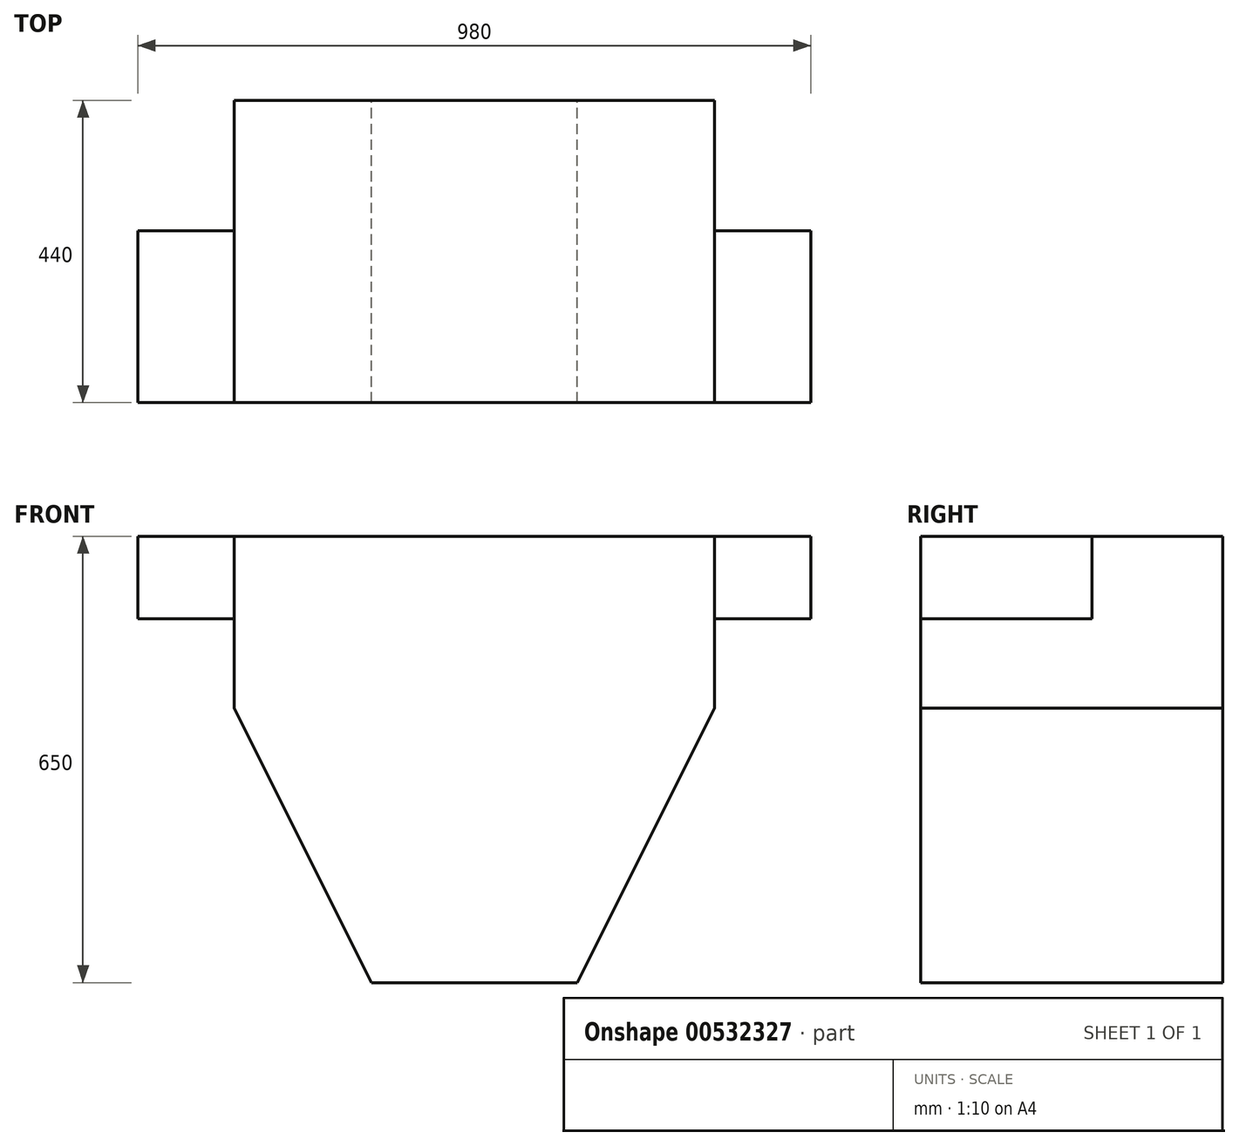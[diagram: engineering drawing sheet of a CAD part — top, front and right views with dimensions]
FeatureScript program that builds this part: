
annotation { "Feature Type Name" : "Feature", "Feature Type Description" : "" }
export const myFeature = defineFeature(function(context is Context, id is Id, definition is map)
    precondition{}
    {
        {
            var Q0;
            Q0=qCreatedBy(makeId("Front.planeOp"),FACE);
            var sketch = newSketch(context, id + "F0", { "sketchPlane" : qUnion([Q0])});
            skLineSegment(sketch, "E0.bottom", {"start": v(350, 325) * mm, "end": v(-350, 325) * mm});
            skLineSegment(sketch, "E0.top", {"start": v(150, -325) * mm, "end": v(-150, -325) * mm});
            skLineSegment(sketch, "E0.left", {"start": v(350, 325) * mm, "end": v(350, 75) * mm});
            skLineSegment(sketch, "E0.right", {"start": v(-350, 325) * mm, "end": v(-350, 75) * mm});
            skPoint(sketch, "E0.middle", {"position": v(0, 0) * mm});
            skLineSegment(sketch, "E1", {"start": v(-150, -325) * mm, "end": v(-350, 75) * mm});
            skLineSegment(sketch, "E2", {"start": v(150, -325) * mm, "end": v(350, 75) * mm});
            skPoint(sketch, "E3.orphan", {"position": v(-350, -325) * mm});
            skPoint(sketch, "E4.orphan", {"position": v(350, -325) * mm});
            skSolve(sketch);
        }
        {
            var Q0;
            Q0 = qSketchRegion(id + "F0", true);
            extrude(context, id + "F1", {"entities" : qUnion([Q0]), "depth" : 440 * mm, "offsetDistance" : 25 * mm});
        }
        {
            var Q0;
            Q0=makeQuery(id+"F1.opExtrude","CAP_FACE",FACE,{"disambiguationData":[OSD([sQuery(id+"F0.wireOp",EDGE,"E0.bottom"),sQuery(id+"F0.wireOp",EDGE,"E0.top"),sQuery(id+"F0.wireOp",EDGE,"E0.left"),sQuery(id+"F0.wireOp",EDGE,"E0.right"),sQuery(id+"F0.wireOp",EDGE,"E1"),sQuery(id+"F0.wireOp",EDGE,"E2")])],"isStart":false});
            var sketch = newSketch(context, id + "F2", { "sketchPlane" : qUnion([Q0])});
            skLineSegment(sketch, "E5.bottom", {"start": v(-350, 325) * mm, "end": v(-490, 325) * mm});
            skLineSegment(sketch, "E5.top", {"start": v(-350, 205) * mm, "end": v(-490, 205) * mm});
            skLineSegment(sketch, "E5.left", {"start": v(-350, 325) * mm, "end": v(-350, 205) * mm});
            skLineSegment(sketch, "E5.right", {"start": v(-490, 325) * mm, "end": v(-490, 205) * mm});
            skSolve(sketch);
        }
        {
            var Q0;
            Q0=makeQuery(id+"F2.imprint","IMPRINT",FACE,{"disambiguationData":[TD([[makeQuery(id+"F2.imprint","IMPRINT",EDGE,{"derivedFrom":sQuery(id+"F2.wireOp",EDGE,"E5.bottom")}),1.0]])]});
            extrude(context, id + "F3", {"entities" : qUnion([Q0]), "oppositeDirection" : true, "depth" : 250 * mm, "offsetDistance" : 25 * mm});
        }
        {
            var Q0;
            Q0=makeQuery(id+"F1.opExtrude","CAP_FACE",FACE,{"disambiguationData":[OSD([sQuery(id+"F0.wireOp",EDGE,"E0.bottom"),sQuery(id+"F0.wireOp",EDGE,"E0.top"),sQuery(id+"F0.wireOp",EDGE,"E0.left"),sQuery(id+"F0.wireOp",EDGE,"E0.right"),sQuery(id+"F0.wireOp",EDGE,"E1"),sQuery(id+"F0.wireOp",EDGE,"E2")])],"isStart":false});
            var sketch = newSketch(context, id + "F4", { "sketchPlane" : qUnion([Q0])});
            skLineSegment(sketch, "E6.bottom", {"start": v(350, 325) * mm, "end": v(490, 325) * mm});
            skLineSegment(sketch, "E6.top", {"start": v(350, 205) * mm, "end": v(490, 205) * mm});
            skLineSegment(sketch, "E6.left", {"start": v(350, 325) * mm, "end": v(350, 205) * mm});
            skLineSegment(sketch, "E6.right", {"start": v(490, 325) * mm, "end": v(490, 205) * mm});
            skSolve(sketch);
        }
        {
            var Q0;
            Q0 = qSketchRegion(id + "F4", true);
            extrude(context, id + "F5", {"entities" : qUnion([Q0]), "oppositeDirection" : true, "depth" : 250 * mm, "offsetDistance" : 25 * mm});
        }
    });
